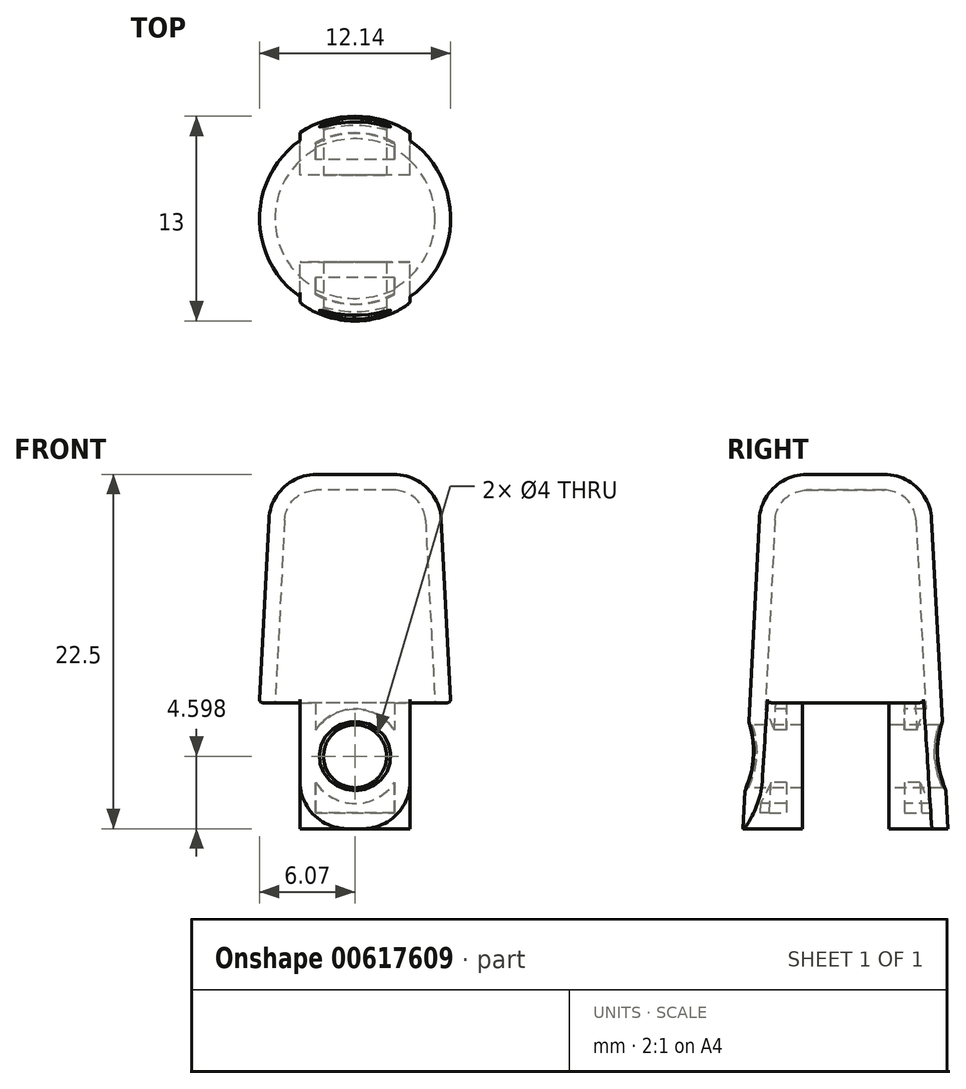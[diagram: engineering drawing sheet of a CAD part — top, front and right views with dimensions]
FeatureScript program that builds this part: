
annotation { "Feature Type Name" : "Feature", "Feature Type Description" : "" }
export const myFeature = defineFeature(function(context is Context, id is Id, definition is map)
    precondition{}
    {
        {
            var Q0;
            Q0=qCreatedBy(makeId("Top.planeOp"),FACE);
            var sketch = newSketch(context, id + "F0", { "sketchPlane" : qUnion([Q0])});
            skCircle(sketch, "E0", {"center": v(0, 0) * mm, "radius": 6.5 * mm});
            skSolve(sketch);
        }
        {
            var Q0;
            Q0 = qSketchRegion(id + "F0", true);
            extrude(context, id + "F1", {"entities" : qUnion([Q0]), "depth" : 22.5 * mm, "offsetDistance" : 25 * mm, "hasDraft" : true, "draftAngle" : 3 * degree, "draftPullDirection" : true});
        }
        {
            var Q0;
            Q0=makeQuery(id+"F1.opExtrude","CAP_EDGE",EDGE,{"disambiguationData":[OSD([sQuery(id+"F0.wireOp",EDGE,"E0")])],"isStart":false});
            fillet(context, id + "F2", {"entities" : qUnion([Q0]), "radius" : 3 * mm, "tangentPropagation" : true, "allowEdgeOverflow" : false});
        }
        {
            var Q0;
            Q0=qCreatedBy(makeId("Top.planeOp"),FACE);
            var sketch = newSketch(context, id + "F3", { "sketchPlane" : qUnion([Q0])});
            skLineSegment(sketch, "E1.bottom", {"start": v(5, -2.75) * mm, "end": v(-5, -2.75) * mm});
            skLineSegment(sketch, "E1.top", {"start": v(5, 2.75) * mm, "end": v(-5, 2.75) * mm});
            skLineSegment(sketch, "E1.left", {"start": v(5, -2.75) * mm, "end": v(5, 2.75) * mm});
            skLineSegment(sketch, "E1.right", {"start": v(-5, -2.75) * mm, "end": v(-5, 2.75) * mm});
            skPoint(sketch, "E1.middle", {"position": v(0, 0) * mm});
            skLineSegment(sketch, "E2.bottom", {"start": v(6.5, -6.25) * mm, "end": v(3.5, -6.25) * mm});
            skLineSegment(sketch, "E2.top", {"start": v(6.5, 6.25) * mm, "end": v(3.5, 6.25) * mm});
            skLineSegment(sketch, "E2.left", {"start": v(6.5, -6.25) * mm, "end": v(6.5, 6.25) * mm});
            skLineSegment(sketch, "E2.right", {"start": v(3.5, -6.25) * mm, "end": v(3.5, 6.25) * mm});
            skPoint(sketch, "E2.middle", {"position": v(5, 0) * mm});
            skLineSegment(sketch, "E3.bottom", {"start": v(-3.5, -6.25) * mm, "end": v(-6.5, -6.25) * mm});
            skLineSegment(sketch, "E3.top", {"start": v(-3.5, 6.25) * mm, "end": v(-6.5, 6.25) * mm});
            skLineSegment(sketch, "E3.left", {"start": v(-3.5, -6.25) * mm, "end": v(-3.5, 6.25) * mm});
            skLineSegment(sketch, "E3.right", {"start": v(-6.5, -6.25) * mm, "end": v(-6.5, 6.25) * mm});
            skPoint(sketch, "E3.middle", {"position": v(-5, 0) * mm});
            skSolve(sketch);
        }
        {
            var Q0;
            Q0 = qSketchRegion(id + "F3", true);
            extrude(context, id + "F4", {"entities" : qUnion([Q0]), "operationType" : NewBodyOperationType.REMOVE, "depth" : 8 * mm, "offsetDistance" : 25 * mm});
        }
        {
            var Q0;
            Q0=makeQuery(id+"F4.boolean.opBoolean","COPY",FACE,{"derivedFrom":makeQuery(id+"F4.opExtrude","SWEPT_FACE",FACE,{"disambiguationData":[OSD([sQuery(id+"F3.wireOp",EDGE,"E1.bottom")])]})});
            var sketch = newSketch(context, id + "F5", { "sketchPlane" : qUnion([Q0])});
            skCircle(sketch, "E4", {"center": v(0, 4.6) * mm, "radius": 2 * mm});
            skPoint(sketch, "E4.centerSnap0", {"position": v(0, 8) * mm});
            skSolve(sketch);
        }
        {
            var Q0;
            Q0 = qSketchRegion(id + "F5", true);
            extrude(context, id + "F6", {"entities" : qUnion([Q0]), "operationType" : NewBodyOperationType.REMOVE, "depth" : 25 * mm, "offsetDistance" : 25 * mm, "hasSecondDirection" : true, "secondDirectionOppositeDirection" : true, "secondDirectionDepth" : 25 * mm});
        }
        {
            var Q0;
            Q0=makeQuery(id+"F4.boolean.opBoolean","COPY",FACE,{"derivedFrom":makeQuery(id+"F4.opExtrude","CAP_FACE",FACE,{"disambiguationData":[OSD([sQuery(id+"F3.wireOp",EDGE,"E1.bottom"),sQuery(id+"F3.wireOp",EDGE,"E1.top"),sQuery(id+"F3.wireOp",EDGE,"E2.bottom"),sQuery(id+"F3.wireOp",EDGE,"E2.top"),sQuery(id+"F3.wireOp",EDGE,"E2.left"),sQuery(id+"F3.wireOp",EDGE,"E2.right"),sQuery(id+"F3.wireOp",EDGE,"E3.bottom"),sQuery(id+"F3.wireOp",EDGE,"E3.top"),sQuery(id+"F3.wireOp",EDGE,"E3.left"),sQuery(id+"F3.wireOp",EDGE,"E3.right")])],"isStart":false})});
            shell(context, id + "F7", {"entities" : qUnion([Q0]), "thickness" : 1 * mm});
        }
        {
            var Q0;
            Q0=makeQuery(id+"F6.boolean.opBoolean","INTERSECT",EDGE,{"disambiguationData":[OD(1.0)],"derivedFrom":[makeQuery(id+"F1.opExtrude","SWEPT_FACE",FACE,{"disambiguationData":[OSD([sQuery(id+"F0.wireOp",EDGE,"E0")])]}),makeQuery(id+"F6.opExtrude","SWEPT_FACE",FACE,{"disambiguationData":[OSD([sQuery(id+"F5.wireOp",EDGE,"E4")])]})]});
            var Q1;
            Q1=makeQuery(id+"F6.boolean.opBoolean","INTERSECT",EDGE,{"disambiguationData":[OD(0.0)],"derivedFrom":[makeQuery(id+"F1.opExtrude","SWEPT_FACE",FACE,{"disambiguationData":[OSD([sQuery(id+"F0.wireOp",EDGE,"E0")])]}),makeQuery(id+"F6.opExtrude","SWEPT_FACE",FACE,{"disambiguationData":[OSD([sQuery(id+"F5.wireOp",EDGE,"E4")])]})]});
            var Q2;
            Q2=makeQuery(id+"F4.boolean.opBoolean","INTERSECT",EDGE,{"disambiguationData":[OD(1.0)],"derivedFrom":[makeQuery(id+"F1.opExtrude","SWEPT_FACE",FACE,{"disambiguationData":[OSD([sQuery(id+"F0.wireOp",EDGE,"E0")])]}),makeQuery(id+"F4.opExtrude","CAP_FACE",FACE,{"disambiguationData":[OSD([sQuery(id+"F3.wireOp",EDGE,"E1.bottom"),sQuery(id+"F3.wireOp",EDGE,"E1.top"),sQuery(id+"F3.wireOp",EDGE,"E2.bottom"),sQuery(id+"F3.wireOp",EDGE,"E2.top"),sQuery(id+"F3.wireOp",EDGE,"E2.left"),sQuery(id+"F3.wireOp",EDGE,"E2.right"),sQuery(id+"F3.wireOp",EDGE,"E3.bottom"),sQuery(id+"F3.wireOp",EDGE,"E3.top"),sQuery(id+"F3.wireOp",EDGE,"E3.left"),sQuery(id+"F3.wireOp",EDGE,"E3.right")])],"isStart":false})]});
            var Q3;
            Q3=makeQuery(id+"F4.boolean.opBoolean","INTERSECT",EDGE,{"disambiguationData":[OD(0.0)],"derivedFrom":[makeQuery(id+"F1.opExtrude","SWEPT_FACE",FACE,{"disambiguationData":[OSD([sQuery(id+"F0.wireOp",EDGE,"E0")])]}),makeQuery(id+"F4.opExtrude","CAP_FACE",FACE,{"disambiguationData":[OSD([sQuery(id+"F3.wireOp",EDGE,"E1.bottom"),sQuery(id+"F3.wireOp",EDGE,"E1.top"),sQuery(id+"F3.wireOp",EDGE,"E2.bottom"),sQuery(id+"F3.wireOp",EDGE,"E2.top"),sQuery(id+"F3.wireOp",EDGE,"E2.left"),sQuery(id+"F3.wireOp",EDGE,"E2.right"),sQuery(id+"F3.wireOp",EDGE,"E3.bottom"),sQuery(id+"F3.wireOp",EDGE,"E3.top"),sQuery(id+"F3.wireOp",EDGE,"E3.left"),sQuery(id+"F3.wireOp",EDGE,"E3.right")])],"isStart":false})]});
            fillet(context, id + "F8", {"entities" : qUnion([Q0, Q1, Q2, Q3]), "radius" : 0.2 * mm, "tangentPropagation" : true, "allowEdgeOverflow" : false});
        }
        {
            var Q0;
            {var subQ0=sQuery(id+"F3.wireOp",EDGE,"E2.right");Q0=makeQuery(id+"F4.boolean.opBoolean","COPY",EDGE,{"derivedFrom":makeQuery(id+"F4.opExtrude","CAP_EDGE",EDGE,{"disambiguationData":[OSD([subQ0]),TDD([makeQuery(id+"F3.imprint","IMPRINT",EDGE,{"disambiguationData":[TD([[makeQuery(id+"F3.imprint","INTERSECT",VERTEX,{"derivedFrom":[sQuery(id+"F3.wireOp",EDGE,"E2.bottom"),subQ0]}),-1.0]])],"derivedFrom":subQ0})])],"isStart":true})});}
            var Q1;
            {var subQ0=sQuery(id+"F3.wireOp",EDGE,"E2.right");Q1=makeQuery(id+"F4.boolean.opBoolean","COPY",EDGE,{"derivedFrom":makeQuery(id+"F4.opExtrude","CAP_EDGE",EDGE,{"disambiguationData":[OSD([subQ0]),TDD([makeQuery(id+"F3.imprint","IMPRINT",EDGE,{"disambiguationData":[TD([[makeQuery(id+"F3.imprint","INTERSECT",VERTEX,{"derivedFrom":[sQuery(id+"F3.wireOp",EDGE,"E2.top"),subQ0]}),1.0]])],"derivedFrom":subQ0})])],"isStart":true})});}
            var Q2;
            {var subQ0=sQuery(id+"F3.wireOp",EDGE,"E3.left");Q2=makeQuery(id+"F4.boolean.opBoolean","COPY",EDGE,{"derivedFrom":makeQuery(id+"F4.opExtrude","CAP_EDGE",EDGE,{"disambiguationData":[OSD([subQ0]),TDD([makeQuery(id+"F3.imprint","IMPRINT",EDGE,{"disambiguationData":[TD([[makeQuery(id+"F3.imprint","INTERSECT",VERTEX,{"derivedFrom":[sQuery(id+"F3.wireOp",EDGE,"E3.top"),subQ0]}),1.0]])],"derivedFrom":subQ0})])],"isStart":true})});}
            var Q3;
            {var subQ0=sQuery(id+"F3.wireOp",EDGE,"E3.left");Q3=makeQuery(id+"F4.boolean.opBoolean","COPY",EDGE,{"derivedFrom":makeQuery(id+"F4.opExtrude","CAP_EDGE",EDGE,{"disambiguationData":[OSD([subQ0]),TDD([makeQuery(id+"F3.imprint","IMPRINT",EDGE,{"disambiguationData":[TD([[makeQuery(id+"F3.imprint","INTERSECT",VERTEX,{"derivedFrom":[sQuery(id+"F3.wireOp",EDGE,"E3.bottom"),subQ0]}),-1.0]])],"derivedFrom":subQ0})])],"isStart":true})});}
            fillet(context, id + "F9", {"entities" : qUnion([Q0, Q1, Q2, Q3]), "radius" : 3 * mm, "tangentPropagation" : true, "allowEdgeOverflow" : false});
        }
    });
